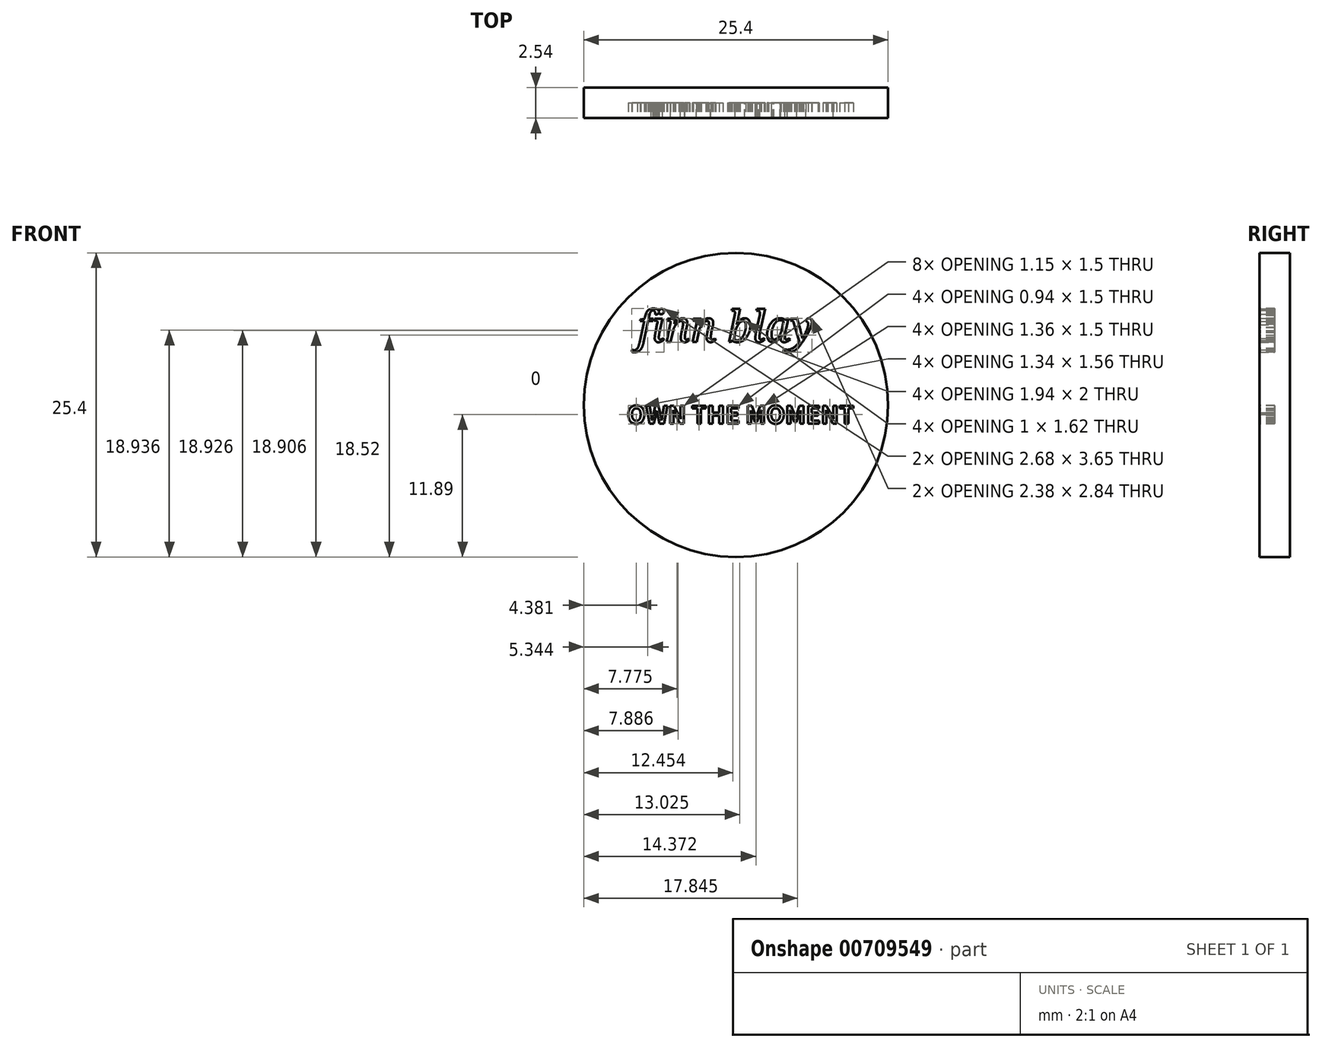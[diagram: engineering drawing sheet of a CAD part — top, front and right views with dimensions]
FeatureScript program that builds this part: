
annotation { "Feature Type Name" : "Feature", "Feature Type Description" : "" }
export const myFeature = defineFeature(function(context is Context, id is Id, definition is map)
    precondition{}
    {
        {
            var Q0;
            Q0=qCreatedBy(makeId("Front.planeOp"),FACE);
            var sketch = newSketch(context, id + "F0", { "sketchPlane" : qUnion([Q0])});
            skCircle(sketch, "E0", {"center": v(0, 0) * mm, "radius": 12.7 * mm});
            skSolve(sketch);
        }
        {
            var Q0;
            Q0=makeQuery(id+"F0.imprint","IMPRINT",FACE,{"disambiguationData":[TD([[makeQuery(id+"F0.imprint","IMPRINT",EDGE,{"derivedFrom":sQuery(id+"F0.wireOp",EDGE,"E0")}),1.0]])]});
            extrude(context, id + "F1", {"entities" : qUnion([Q0]), "depth" : 2.54 * mm, "offsetDistance" : 25.4 * mm});
        }
        {
            var Q0;
            Q0=makeQuery(id+"F1.opExtrude","CAP_FACE",FACE,{"disambiguationData":[OSD([sQuery(id+"F0.wireOp",EDGE,"E0")])],"isStart":false});
            var sketch = newSketch(context, id + "F2", { "sketchPlane" : qUnion([Q0])});
            skText(sketch, "E1", { "text": "finn blay", "fontName": "NotoSerif-Italic.ttf"});
            const initialGuessF2  = {"E1": [-0.00819, 0.00527, 1, 0, 0.0026]};
            skSetInitialGuess(sketch, initialGuessF2);
            skSolve(sketch);
        }
        {
            var Q0;
            Q0 = qSketchRegion(id + "F2", true);
            extrude(context, id + "F3", {"entities" : qUnion([Q0]), "operationType" : NewBodyOperationType.REMOVE, "oppositeDirection" : true, "depth" : 1.27 * mm, "offsetDistance" : 25.4 * mm});
        }
        {
            var Q0;
            {var subQ0=sQuery(id+"F0.wireOp",EDGE,"E0");Q0=makeQuery(id+"F3.boolean.opBoolean","SPLIT",FACE,{"disambiguationData":[TD([makeQuery(id+"F1.opExtrude","SWEPT_FACE",FACE,{"disambiguationData":[OSD([subQ0])]})])],"derivedFrom":makeQuery(id+"F1.opExtrude","CAP_FACE",FACE,{"disambiguationData":[OSD([subQ0])],"isStart":false})});}
            var sketch = newSketch(context, id + "F4", { "sketchPlane" : qUnion([Q0])});
            skText(sketch, "E2", { "text": "OWN THE MOMENT", "fontName": "NotoSansCJKkr-Bold.otf"});
            const initialGuessF4  = {"E2": [-0.0091, -0.00156, 1, 0, 0.00146]};
            skSetInitialGuess(sketch, initialGuessF4);
            skSolve(sketch);
        }
        {
            var Q0;
            Q0 = qSketchRegion(id + "F4", true);
            extrude(context, id + "F5", {"entities" : qUnion([Q0]), "operationType" : NewBodyOperationType.REMOVE, "oppositeDirection" : true, "depth" : 1.27 * mm, "offsetDistance" : 25.4 * mm});
        }
    });
